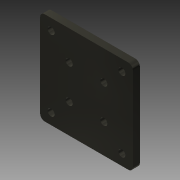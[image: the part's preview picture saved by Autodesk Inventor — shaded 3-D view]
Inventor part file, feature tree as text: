
AUTODESK INVENTOR PART (.ipt)
format: ipt  version: 2015 (Build 190159000, 159)  size: 116,224 bytes
history: native  units: mm
features: extrude x1, fillet x1, sketch x1
ambient origin geometry x8: Origin, YZ Plane, XZ Plane, XY Plane, X Axis, Y Axis, Z Axis, Center Point
bodies: Body1 (feature_tree)
feature tree (3):
  extrude  "Extrusion3"  Depth=36.0mm
  fillet  "Fillet2"  Radius=40.0mm
  sketch  "Sketch1"  dims[d0=36.0mm d1=36.0mm d50=40.0mm d51=40.0mm d55=3.0mm d56=3.0mm d57=3.0mm d58=3.0mm d59=3.0mm d60=0.0mm d61=2.0mm]
